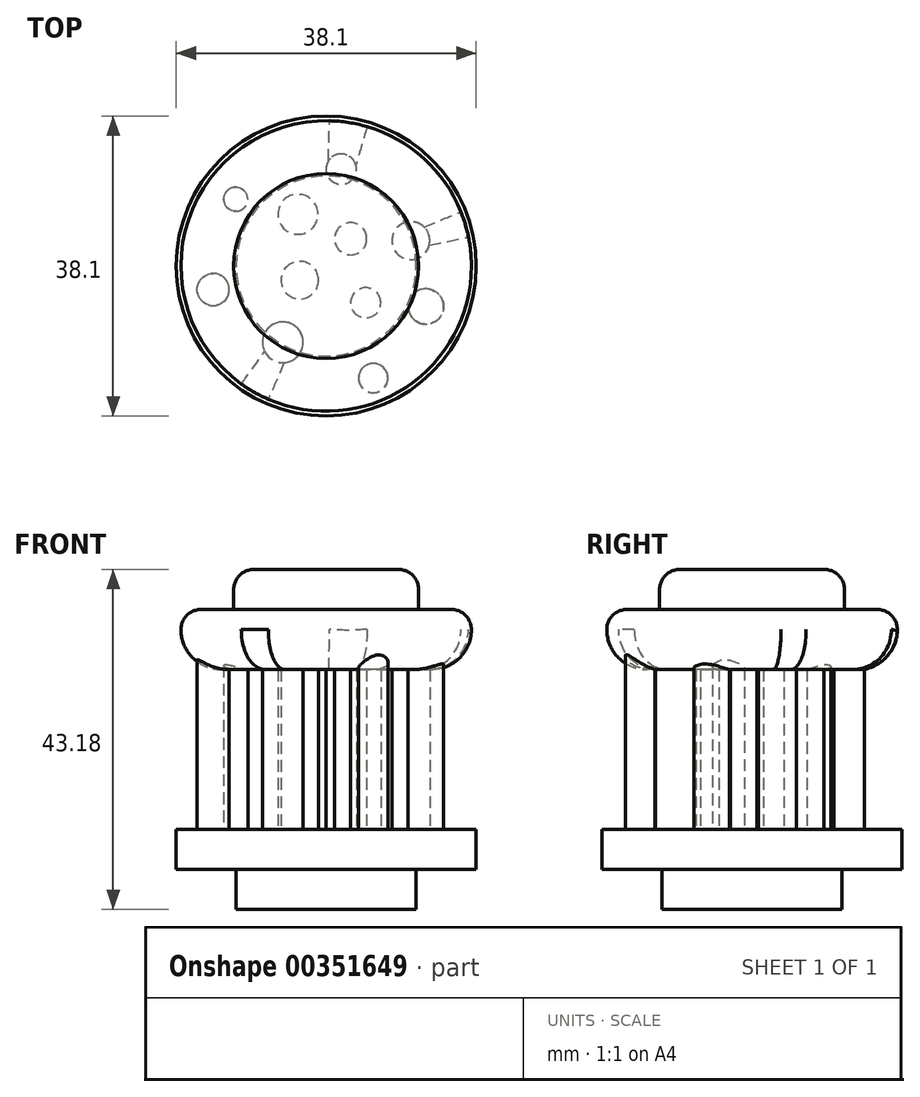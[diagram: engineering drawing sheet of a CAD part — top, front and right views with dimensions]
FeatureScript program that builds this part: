
annotation { "Feature Type Name" : "Feature", "Feature Type Description" : "" }
export const myFeature = defineFeature(function(context is Context, id is Id, definition is map)
    precondition{}
    {
        {
            var Q0;
            Q0=qCreatedBy(makeId("Top.planeOp"),FACE);
            var sketch = newSketch(context, id + "F0", { "sketchPlane" : qUnion([Q0])});
            skCircle(sketch, "E0", {"center": v(0, 0) * mm, "radius": 11.43 * mm});
            skSolve(sketch);
        }
        {
            var Q0;
            Q0 = qSketchRegion(id + "F0", true);
            extrude(context, id + "F1", {"entities" : qUnion([Q0]), "depth" : 5.08 * mm});
        }
        {
            var Q0;
            Q0=makeQuery(id+"F1.opExtrude","CAP_FACE",FACE,{"disambiguationData":[OSD([sQuery(id+"F0.wireOp",EDGE,"E0")])],"isStart":false});
            var sketch = newSketch(context, id + "F2", { "sketchPlane" : qUnion([Q0])});
            skCircle(sketch, "E1", {"center": v(0, 0) * mm, "radius": 19.05 * mm});
            skSolve(sketch);
        }
        {
            var Q0;
            Q0 = qSketchRegion(id + "F2", true);
            extrude(context, id + "F3", {"entities" : qUnion([Q0]), "operationType" : NewBodyOperationType.ADD, "depth" : 5.08 * mm});
        }
        {
            var Q0;
            Q0=makeQuery(id+"F3.opExtrude","CAP_FACE",FACE,{"disambiguationData":[OSD([sQuery(id+"F2.wireOp",EDGE,"E1")])],"isStart":false});
            var sketch = newSketch(context, id + "F4", { "sketchPlane" : qUnion([Q0])});
            skCircle(sketch, "E2", {"center": v(-11.48, 8.5) * mm, "radius": 1.53 * mm});
            skCircle(sketch, "E3", {"center": v(1.91, 12.32) * mm, "radius": 1.93 * mm});
            skCircle(sketch, "E4", {"center": v(-3.59, 6.58) * mm, "radius": 2.54 * mm});
            skCircle(sketch, "E5", {"center": v(10.76, 3.23) * mm, "radius": 2.4 * mm});
            skCircle(sketch, "E6", {"center": v(5.02, -4.66) * mm, "radius": 1.91 * mm});
            skCircle(sketch, "E7", {"center": v(-14.35, -2.99) * mm, "radius": 2.04 * mm});
            skCircle(sketch, "E8", {"center": v(-5.5, -9.69) * mm, "radius": 2.59 * mm});
            skCircle(sketch, "E9", {"center": v(5.98, -14.23) * mm, "radius": 1.87 * mm});
            skCircle(sketch, "E10", {"center": v(-3.35, -1.8) * mm, "radius": 2.4 * mm});
            skCircle(sketch, "E11", {"center": v(3.1, 3.47) * mm, "radius": 2.04 * mm});
            skCircle(sketch, "E12", {"center": v(12.68, -5.14) * mm, "radius": 2.26 * mm});
            skSolve(sketch);
        }
        {
            var Q0;
            Q0 = qSketchRegion(id + "F4", true);
            extrude(context, id + "F5", {"entities" : qUnion([Q0]), "operationType" : NewBodyOperationType.ADD, "depth" : 20.32 * mm});
        }
        {
            var Q0;
            Q0=makeQuery(id+"F5.opExtrude","CAP_FACE",FACE,{"disambiguationData":[OSD([sQuery(id+"F4.wireOp",EDGE,"E4")])],"isStart":false});
            var sketch = newSketch(context, id + "F6", { "sketchPlane" : qUnion([Q0])});
            skCircle(sketch, "E13", {"center": v(0, 0) * mm, "radius": 18.45 * mm});
            skSolve(sketch);
        }
        {
            var Q0;
            Q0 = qSketchRegion(id + "F6", true);
            extrude(context, id + "F7", {"entities" : qUnion([Q0]), "operationType" : NewBodyOperationType.ADD, "depth" : 7.62 * mm});
        }
        {
            var Q0;
            Q0=makeQuery(id+"F7.opExtrude","CAP_FACE",FACE,{"disambiguationData":[OSD([sQuery(id+"F6.wireOp",EDGE,"E13")])],"isStart":false});
            var sketch = newSketch(context, id + "F8", { "sketchPlane" : qUnion([Q0])});
            skCircle(sketch, "E14", {"center": v(0, 0) * mm, "radius": 11.75 * mm});
            skSolve(sketch);
        }
        {
            var Q0;
            Q0 = qSketchRegion(id + "F8", true);
            extrude(context, id + "F9", {"entities" : qUnion([Q0]), "operationType" : NewBodyOperationType.ADD, "depth" : 5.08 * mm});
        }
        {
            var Q0;
            Q0=makeQuery(id+"F9.opExtrude","CAP_EDGE",EDGE,{"disambiguationData":[OSD([sQuery(id+"F8.wireOp",EDGE,"E14")])],"isStart":false});
            var Q1;
            Q1=makeQuery(id+"F7.opExtrude","CAP_EDGE",EDGE,{"disambiguationData":[OSD([sQuery(id+"F6.wireOp",EDGE,"E13")])],"isStart":false});
            fillet(context, id + "F10", {"entities" : qUnion([Q0, Q1]), "radius" : 2.54 * mm, "tangentPropagation" : true, "allowEdgeOverflow" : false});
        }
        {
            var Q0;
            Q0=makeQuery(id+"F7.opExtrude","CAP_EDGE",EDGE,{"disambiguationData":[OSD([sQuery(id+"F6.wireOp",EDGE,"E13")])],"isStart":true});
            fillet(context, id + "F11", {"entities" : qUnion([Q0]), "radius" : 5.08 * mm, "tangentPropagation" : true, "allowEdgeOverflow" : false});
        }
    });
